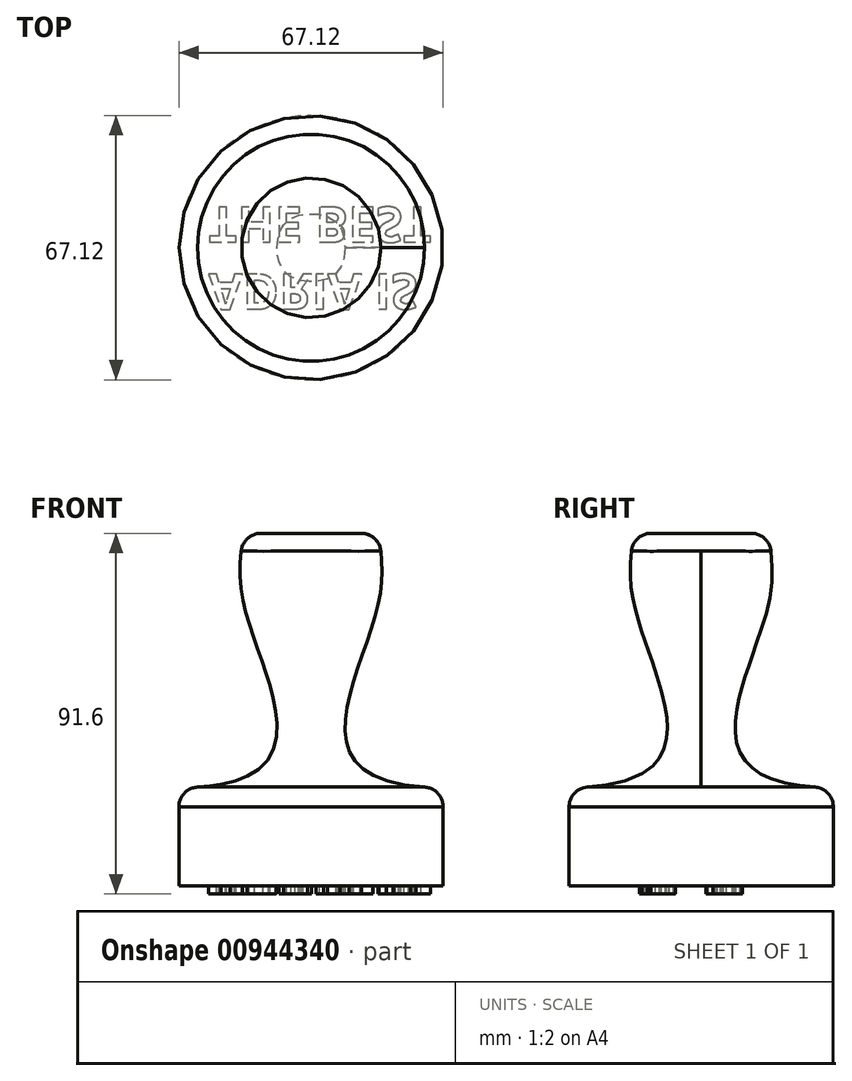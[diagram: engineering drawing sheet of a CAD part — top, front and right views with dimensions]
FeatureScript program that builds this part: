
annotation { "Feature Type Name" : "Feature", "Feature Type Description" : "" }
export const myFeature = defineFeature(function(context is Context, id is Id, definition is map)
    precondition{}
    {
        {
            var Q0;
            Q0=qCreatedBy(makeId("Top.planeOp"),FACE);
            cPlane(context, id + "F0", {"entities" : qUnion([Q0]), "cplaneType" : CPlaneType.OFFSET, "offset" : 47.4 * mm, "width" : 150 * mm, "height" : 150 * mm});
        }
        {
            var Q0;
            Q0=qCreatedBy(id+"F0.planeOp",FACE);
            cPlane(context, id + "F1", {"entities" : qUnion([Q0]), "cplaneType" : CPlaneType.OFFSET, "offset" : 17.2 * mm, "width" : 150 * mm, "height" : 150 * mm});
        }
        {
            var Q0;
            Q0=qCreatedBy(makeId("Top.planeOp"),FACE);
            var sketch = newSketch(context, id + "F2", { "sketchPlane" : qUnion([Q0])});
            skCircle(sketch, "E0", {"center": v(0, 0) * mm, "radius": 33.5 * mm});
            skSolve(sketch);
        }
        {
            var Q0;
            Q0=qCreatedBy(id+"F0.planeOp",FACE);
            var sketch = newSketch(context, id + "F3", { "sketchPlane" : qUnion([Q0])});
            skCircle(sketch, "E1", {"center": v(0, 0) * mm, "radius": 17.26 * mm});
            skSolve(sketch);
        }
        {
            var Q0;
            Q0=qCreatedBy(id+"F1.planeOp",FACE);
            var sketch = newSketch(context, id + "F4", { "sketchPlane" : qUnion([Q0])});
            skCircle(sketch, "E2", {"center": v(0, 0) * mm, "radius": 17.23 * mm});
            skSolve(sketch);
        }
        {
            var Q0;
            Q0=makeQuery(id+"F4.imprint","IMPRINT",FACE,{"disambiguationData":[TD([[makeQuery(id+"F4.imprint","IMPRINT",EDGE,{"derivedFrom":sQuery(id+"F4.wireOp",EDGE,"E2")}),1.0]])]});
            var Q1;
            Q1=makeQuery(id+"F3.imprint","IMPRINT",FACE,{"disambiguationData":[TD([[makeQuery(id+"F3.imprint","IMPRINT",EDGE,{"derivedFrom":sQuery(id+"F3.wireOp",EDGE,"E1")}),1.0]])]});
            var Q2;
            Q2=makeQuery(id+"F2.imprint","IMPRINT",FACE,{"disambiguationData":[TD([[makeQuery(id+"F2.imprint","IMPRINT",EDGE,{"derivedFrom":sQuery(id+"F2.wireOp",EDGE,"E0")}),1.0]])]});
            loft(context, id + "F5", {"endCondition" : LoftEndDerivativeType.TANGENT_TO_PROFILE, "endMagnitude" : 5.5, "sheetProfilesArray" : [{ "sheetProfileEntities" : qUnion([Q0]) }, { "sheetProfileEntities" : qUnion([Q1]) }, { "sheetProfileEntities" : qUnion([Q2]) }]});
        }
        {
            var Q0;
            Q0=makeQuery(id+"F5.opLoft","CAP_FACE",FACE,{"disambiguationData":[OSD([makeQuery(id+"F2.imprint","IMPRINT",FACE,{"disambiguationData":[TD([[makeQuery(id+"F2.imprint","IMPRINT",EDGE,{"derivedFrom":sQuery(id+"F2.wireOp",EDGE,"E0")}),1.0]])]})])],"isStart":true});
            var sketch = newSketch(context, id + "F6", { "sketchPlane" : qUnion([Q0])});
            skCircle(sketch, "E3", {"center": v(0, 0) * mm, "radius": 33.56 * mm});
            skSolve(sketch);
        }
        {
            var Q0;
            Q0 = qSketchRegion(id + "F6", true);
            extrude(context, id + "F7", {"entities" : qUnion([Q0]), "operationType" : NewBodyOperationType.ADD, "depth" : 25 * mm, "offsetDistance" : 25 * mm});
        }
        {
            var Q0;
            Q0=makeQuery(id+"F7.opExtrude","CAP_FACE",FACE,{"disambiguationData":[OSD([sQuery(id+"F6.wireOp",EDGE,"E3")])],"isStart":false});
            var sketch = newSketch(context, id + "F8", { "sketchPlane" : qUnion([Q0])});
            skText(sketch, "E4", { "text": "ADRIA IS \nTHE BEST", "fontName": "OpenSans-Bold.ttf"});
            const initialGuessF8  = {"E4": [-0.02602, 0.00668, 1, 0, 0.009]};
            skSetInitialGuess(sketch, initialGuessF8);
            skSolve(sketch);
        }
        {
            var Q0;
            Q0 = qSketchRegion(id + "F8", true);
            extrude(context, id + "F9", {"entities" : qUnion([Q0]), "operationType" : NewBodyOperationType.ADD, "depth" : 2 * mm, "offsetDistance" : 25 * mm});
        }
        {
            var Q0;
            Q0=makeQuery(id+"F5.opLoft","MID_CAP_EDGE",EDGE,{"disambiguationData":[OSD([sQuery(id+"F4.wireOp",EDGE,"E2")])],"capPos":0.0});
            fillet(context, id + "F10", {"entities" : qUnion([Q0]), "radius" : 5 * mm, "tangentPropagation" : true, "allowEdgeOverflow" : false});
        }
        {
            var Q0;
            Q0=makeQuery(id+"F7.opExtrude","CAP_EDGE",EDGE,{"disambiguationData":[OSD([sQuery(id+"F6.wireOp",EDGE,"E3")])],"isStart":true});
            fillet(context, id + "F11", {"entities" : qUnion([Q0]), "radius" : 5 * mm, "tangentPropagation" : true, "allowEdgeOverflow" : false});
        }
    });
